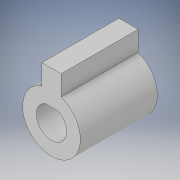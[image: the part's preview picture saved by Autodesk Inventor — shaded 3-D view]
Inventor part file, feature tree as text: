
AUTODESK INVENTOR PART (.ipt)
format: ipt  version: 2017 (Build 210142000, 142)  size: 107,520 bytes
history: native  units: in
note: dims shown in document units (in); Inventor stores cm internally (conversion verified against a paired STEP export)
features: extrude x2, sketch x2
ambient origin geometry x8: Origin, YZ Plane, XZ Plane, XY Plane, X Axis, Y Axis, Z Axis, Center Point
bodies: Solid1 (feature_tree)
feature tree (4):
  extrude  "Extrusion1"  Depth=0.25in
  extrude  "Extrusion2"  Depth=0.3937in
  sketch  "Sketch1"  dims[d0=0.75in d1=0.25in]
  sketch  "Sketch2"  dims[d5=1.0in d6=0.0in d7=0.3937in d8=0.374in d9=1.0in d10=0.0in]
